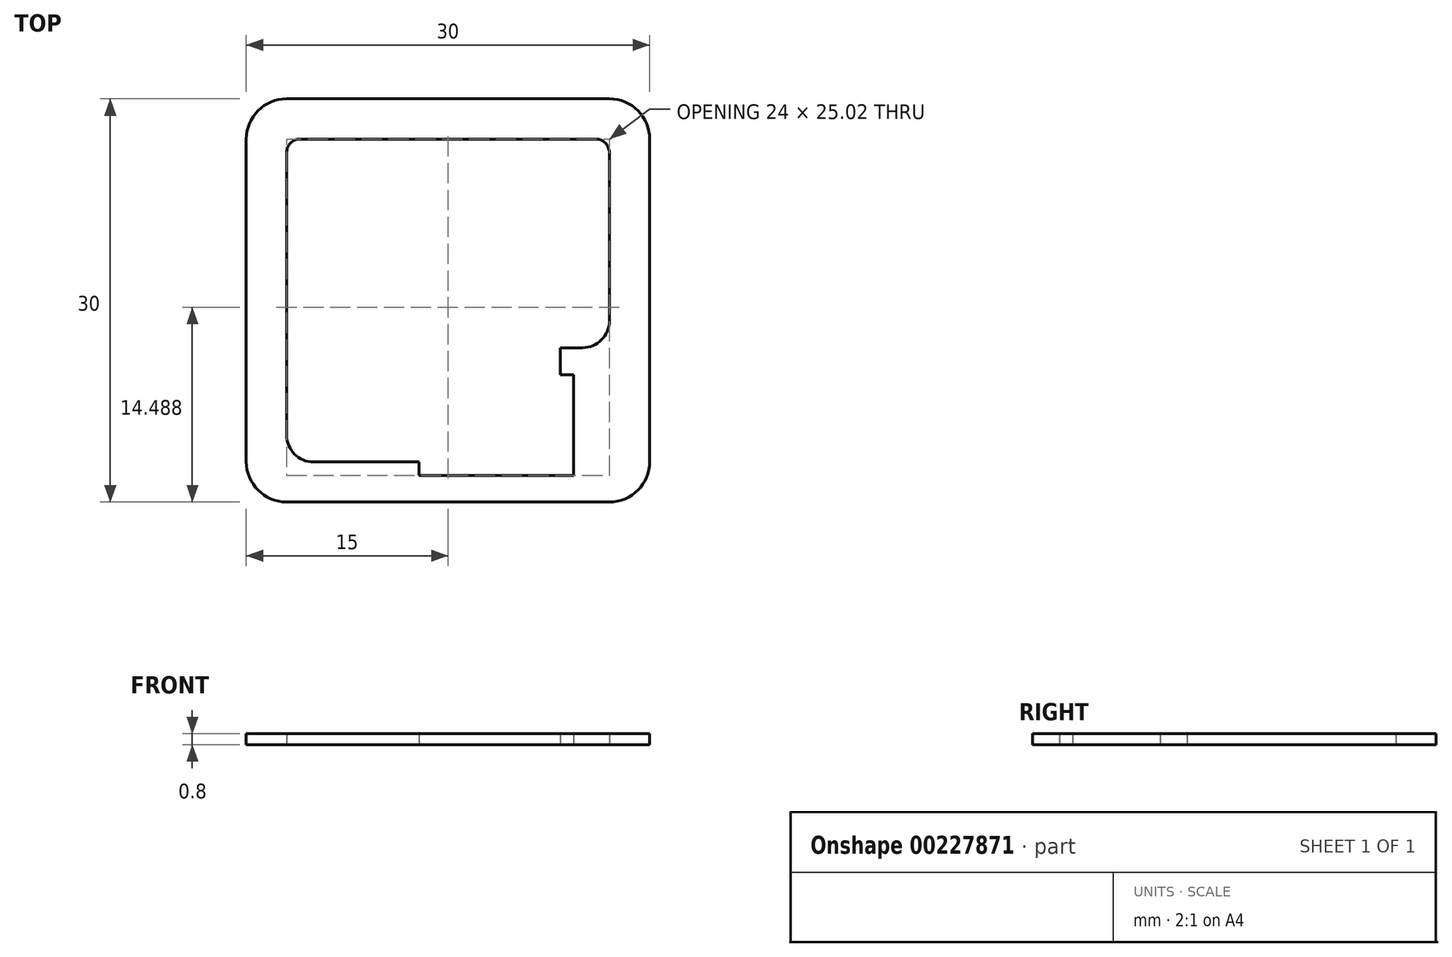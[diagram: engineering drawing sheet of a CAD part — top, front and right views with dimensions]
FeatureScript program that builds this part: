
annotation { "Feature Type Name" : "Feature", "Feature Type Description" : "" }
export const myFeature = defineFeature(function(context is Context, id is Id, definition is map)
    precondition{}
    {
        {
            var Q0;
            Q0=qCreatedBy(makeId("Top.planeOp"),FACE);
            var sketch = newSketch(context, id + "F0", { "sketchPlane" : qUnion([Q0])});
            skLineSegment(sketch, "E0.bottom", {"start": v(12, 15) * mm, "end": v(-12, 15) * mm});
            skLineSegment(sketch, "E0.top", {"start": v(12, -15) * mm, "end": v(-12, -15) * mm});
            skLineSegment(sketch, "E0.left", {"start": v(15, 12) * mm, "end": v(15, -12) * mm});
            skLineSegment(sketch, "E0.right", {"start": v(-15, 12) * mm, "end": v(-15, -12) * mm});
            skPoint(sketch, "E0.middle", {"position": v(0, 0) * mm});
            skPoint(sketch, "E1.visualSharp", {"position": v(-15, 15) * mm});
            skArc(sketch, "E1.filletArc", {"start": v(-12, 15) * mm, "mid": v(-14.12, 14.12) * mm, "end": v(-15, 12) * mm});
            skPoint(sketch, "E2.visualSharp", {"position": v(15, 15) * mm});
            skArc(sketch, "E2.filletArc", {"start": v(15, 12) * mm, "mid": v(14.12, 14.12) * mm, "end": v(12, 15) * mm});
            skPoint(sketch, "E3.visualSharp", {"position": v(15, -15) * mm});
            skArc(sketch, "E3.filletArc", {"start": v(12, -15) * mm, "mid": v(14.12, -14.12) * mm, "end": v(15, -12) * mm});
            skPoint(sketch, "E4.visualSharp", {"position": v(-15, -15) * mm});
            skArc(sketch, "E4.filletArc", {"start": v(-15, -12) * mm, "mid": v(-14.12, -14.12) * mm, "end": v(-12, -15) * mm});
            skLineSegment(sketch, "E5.bottom", {"start": v(-2.15, -13.03) * mm, "end": v(9.35, -13.03) * mm});
            skLineSegment(sketch, "E5.top", {"start": v(8.35, -5.53) * mm, "end": v(9.35, -5.53) * mm});
            skLineSegment(sketch, "E5.left", {"start": v(-2.15, -13.03) * mm, "end": v(-2.15, -12.03) * mm});
            skLineSegment(sketch, "E5.right", {"start": v(9.35, -13.03) * mm, "end": v(9.35, -5.53) * mm});
            skLineSegment(sketch, "E6.bottom", {"start": v(-11, 12) * mm, "end": v(11, 12) * mm});
            skLineSegment(sketch, "E6.top", {"start": v(-10, -12.03) * mm, "end": v(-2.15, -12.03) * mm});
            skLineSegment(sketch, "E6.left", {"start": v(-12, 11) * mm, "end": v(-12, -10.03) * mm});
            skLineSegment(sketch, "E6.right", {"start": v(8.35, -3.53) * mm, "end": v(8.35, -5.53) * mm});
            skLineSegment(sketch, "E7", {"start": v(8.35, -5.53) * mm, "end": v(8.35, -3.53) * mm});
            skLineSegment(sketch, "E8", {"start": v(8.35, -3.53) * mm, "end": v(10, -3.53) * mm});
            skLineSegment(sketch, "E9", {"start": v(12, -1.53) * mm, "end": v(12, 11) * mm});
            skPoint(sketch, "E10.visualSharp", {"position": v(12, -3.53) * mm});
            skArc(sketch, "E10.filletArc", {"start": v(10, -3.53) * mm, "mid": v(11.41, -2.94) * mm, "end": v(12, -1.53) * mm});
            skPoint(sketch, "E11.visualSharp", {"position": v(-12, -12.03) * mm});
            skArc(sketch, "E11.filletArc", {"start": v(-12, -10.03) * mm, "mid": v(-11.41, -11.44) * mm, "end": v(-10, -12.03) * mm});
            skArc(sketch, "E12", {"start": v(-11, 12) * mm, "mid": v(-11.7, 11.7) * mm, "end": v(-12, 11) * mm});
            skArc(sketch, "E13", {"start": v(12, 11) * mm, "mid": v(11.7, 11.7) * mm, "end": v(11, 12) * mm});
            skSolve(sketch);
        }
        {
            var Q0;
            Q0=makeQuery(id+"F0.imprint","IMPRINT",FACE,{"disambiguationData":[TD([[makeQuery(id+"F0.imprint","IMPRINT",EDGE,{"derivedFrom":sQuery(id+"F0.wireOp",EDGE,"E0.bottom")}),1.0]])]});
            extrude(context, id + "F1", {"entities" : qUnion([Q0]), "depth" : 0.8 * mm});
        }
    });
